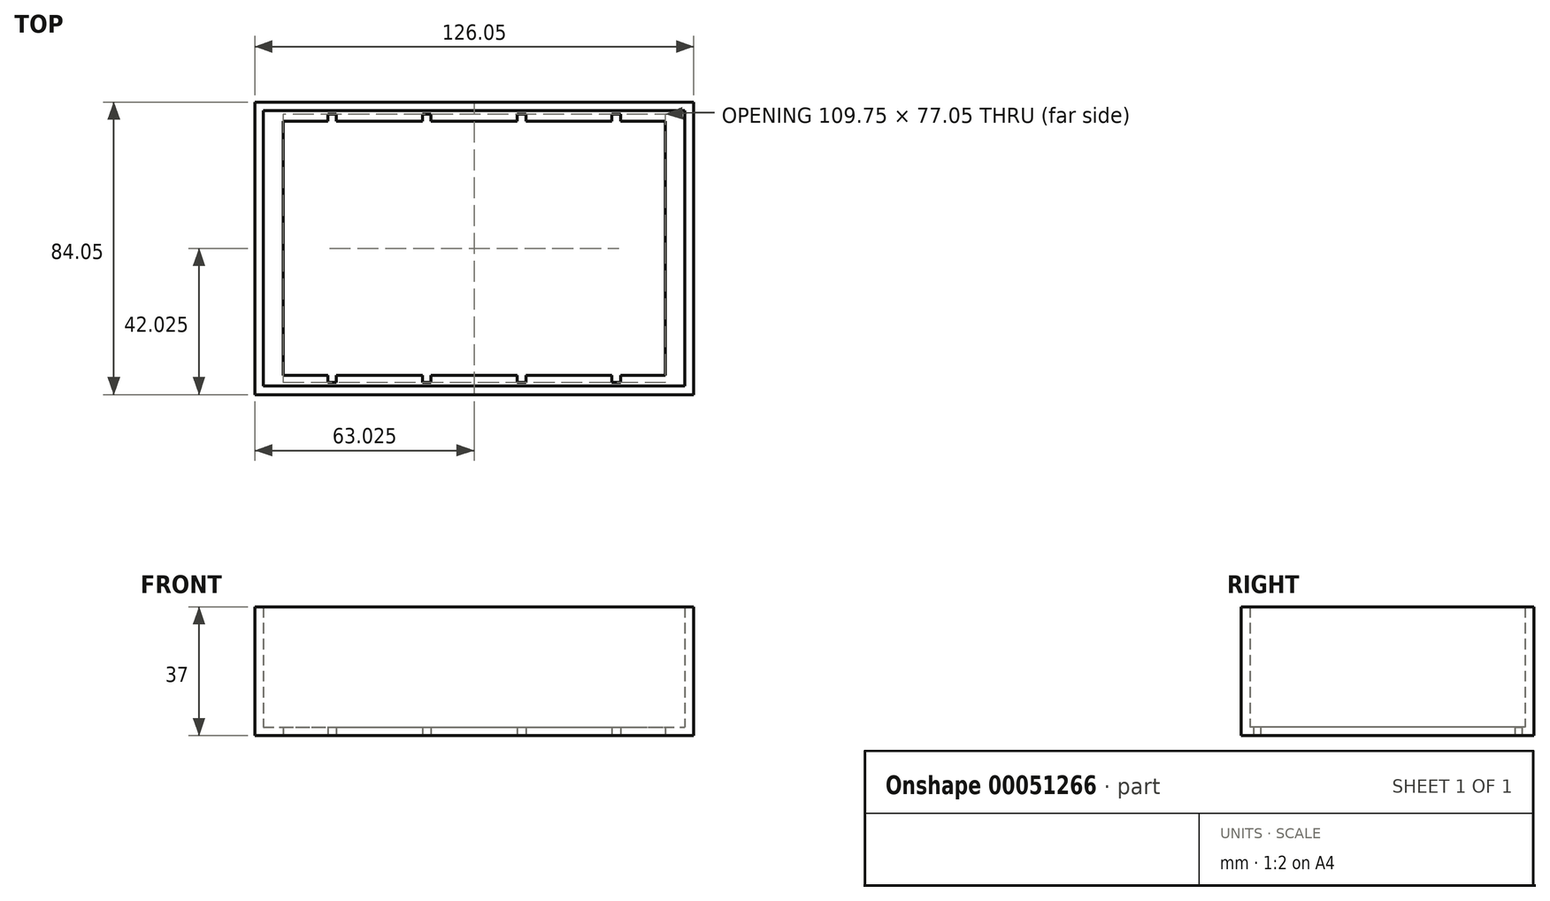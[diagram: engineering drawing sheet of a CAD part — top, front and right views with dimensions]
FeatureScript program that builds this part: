
annotation { "Feature Type Name" : "Feature", "Feature Type Description" : "" }
export const myFeature = defineFeature(function(context is Context, id is Id, definition is map)
    precondition{}
    {
        {
            var Q0;
            Q0=qCreatedBy(makeId("Top.planeOp"),FACE);
            var sketch = newSketch(context, id + "F0", { "sketchPlane" : qUnion([Q0])});
            skLineSegment(sketch, "E0.bottom", {"start": v(0, 0) * mm, "end": v(126.05, 0) * mm});
            skLineSegment(sketch, "E0.top", {"start": v(0, -84.05) * mm, "end": v(126.05, -84.05) * mm});
            skLineSegment(sketch, "E0.left", {"start": v(0, 0) * mm, "end": v(0, -84.05) * mm});
            skLineSegment(sketch, "E0.right", {"start": v(126.05, 0) * mm, "end": v(126.05, -84.05) * mm});
            skLineSegment(sketch, "E1.bottom", {"start": v(2.5, -2.5) * mm, "end": v(123.55, -2.5) * mm});
            skLineSegment(sketch, "E1.top", {"start": v(2.5, -81.55) * mm, "end": v(123.55, -81.55) * mm});
            skLineSegment(sketch, "E1.left", {"start": v(2.5, -2.5) * mm, "end": v(2.5, -81.55) * mm});
            skLineSegment(sketch, "E1.right", {"start": v(123.55, -2.5) * mm, "end": v(123.55, -81.55) * mm});
            skLineSegment(sketch, "E2.bottom", {"start": v(8.15, -5.5) * mm, "end": v(117.9, -5.5) * mm});
            skLineSegment(sketch, "E2.top", {"start": v(8.15, -78.55) * mm, "end": v(117.9, -78.55) * mm});
            skLineSegment(sketch, "E2.left", {"start": v(8.15, -5.5) * mm, "end": v(8.15, -78.55) * mm});
            skLineSegment(sketch, "E2.right", {"start": v(117.9, -5.5) * mm, "end": v(117.9, -78.55) * mm});
            skLineSegment(sketch, "E3.bottom", {"start": v(20.95, -78.55) * mm, "end": v(23.45, -78.55) * mm});
            skLineSegment(sketch, "E3.top", {"start": v(20.95, -80.55) * mm, "end": v(23.45, -80.55) * mm});
            skLineSegment(sketch, "E3.left", {"start": v(20.95, -78.55) * mm, "end": v(20.95, -80.55) * mm});
            skLineSegment(sketch, "E3.right", {"start": v(23.45, -78.55) * mm, "end": v(23.45, -80.55) * mm});
            skLineSegment(sketch, "E4.bottom", {"start": v(20.95, -5.5) * mm, "end": v(23.45, -5.5) * mm});
            skLineSegment(sketch, "E4.top", {"start": v(20.95, -3.5) * mm, "end": v(23.45, -3.5) * mm});
            skLineSegment(sketch, "E4.left", {"start": v(20.95, -5.5) * mm, "end": v(20.95, -3.5) * mm});
            skLineSegment(sketch, "E4.right", {"start": v(23.45, -5.5) * mm, "end": v(23.45, -3.5) * mm});
            skLineSegment(sketch, "E5.bottom", {"start": v(102.6, -78.55) * mm, "end": v(105.1, -78.55) * mm});
            skLineSegment(sketch, "E5.top", {"start": v(102.6, -80.55) * mm, "end": v(105.1, -80.55) * mm});
            skLineSegment(sketch, "E5.left", {"start": v(105.1, -78.55) * mm, "end": v(105.1, -80.55) * mm});
            skLineSegment(sketch, "E5.right", {"start": v(102.6, -78.55) * mm, "end": v(102.6, -80.55) * mm});
            skLineSegment(sketch, "E6.bottom", {"start": v(102.6, -5.5) * mm, "end": v(105.1, -5.5) * mm});
            skLineSegment(sketch, "E6.top", {"start": v(102.6, -3.5) * mm, "end": v(105.1, -3.5) * mm});
            skLineSegment(sketch, "E6.left", {"start": v(102.6, -5.5) * mm, "end": v(102.6, -3.5) * mm});
            skLineSegment(sketch, "E6.right", {"start": v(105.1, -5.5) * mm, "end": v(105.1, -3.5) * mm});
            skLineSegment(sketch, "E7.bottom", {"start": v(48.15, -78.55) * mm, "end": v(50.65, -78.55) * mm});
            skLineSegment(sketch, "E7.top", {"start": v(48.15, -80.55) * mm, "end": v(50.65, -80.55) * mm});
            skLineSegment(sketch, "E7.left", {"start": v(48.15, -78.55) * mm, "end": v(48.15, -80.55) * mm});
            skLineSegment(sketch, "E7.right", {"start": v(50.65, -78.55) * mm, "end": v(50.65, -80.55) * mm});
            skLineSegment(sketch, "E8.bottom", {"start": v(75.4, -78.55) * mm, "end": v(77.9, -78.55) * mm});
            skLineSegment(sketch, "E8.top", {"start": v(75.4, -80.55) * mm, "end": v(77.9, -80.55) * mm});
            skLineSegment(sketch, "E8.left", {"start": v(75.4, -78.55) * mm, "end": v(75.4, -80.55) * mm});
            skLineSegment(sketch, "E8.right", {"start": v(77.9, -78.55) * mm, "end": v(77.9, -80.55) * mm});
            skLineSegment(sketch, "E9.bottom", {"start": v(48.15, -5.5) * mm, "end": v(50.65, -5.5) * mm});
            skLineSegment(sketch, "E9.top", {"start": v(48.15, -3.5) * mm, "end": v(50.65, -3.5) * mm});
            skLineSegment(sketch, "E9.left", {"start": v(48.15, -5.5) * mm, "end": v(48.15, -3.5) * mm});
            skLineSegment(sketch, "E9.right", {"start": v(50.65, -5.5) * mm, "end": v(50.65, -3.5) * mm});
            skLineSegment(sketch, "E10.bottom", {"start": v(75.4, -5.5) * mm, "end": v(77.9, -5.5) * mm});
            skLineSegment(sketch, "E10.top", {"start": v(75.4, -3.5) * mm, "end": v(77.9, -3.5) * mm});
            skLineSegment(sketch, "E10.left", {"start": v(75.4, -5.5) * mm, "end": v(75.4, -3.5) * mm});
            skLineSegment(sketch, "E10.right", {"start": v(77.9, -5.5) * mm, "end": v(77.9, -3.5) * mm});
            skSolve(sketch);
        }
        {
            var Q0;
            Q0=makeQuery(id+"F0.imprint","IMPRINT",FACE,{"disambiguationData":[TD([[makeQuery(id+"F0.imprint","IMPRINT",EDGE,{"derivedFrom":sQuery(id+"F0.wireOp",EDGE,"E1.bottom")}),-1.0]])]});
            extrude(context, id + "F1", {"entities" : qUnion([Q0]), "depth" : 2.5 * mm});
        }
        {
            var Q0;
            Q0=makeQuery(id+"F0.imprint","IMPRINT",FACE,{"disambiguationData":[TD([[makeQuery(id+"F0.imprint","IMPRINT",EDGE,{"derivedFrom":sQuery(id+"F0.wireOp",EDGE,"E0.bottom")}),-1.0]])]});
            extrude(context, id + "F2", {"entities" : qUnion([Q0]), "operationType" : NewBodyOperationType.ADD, "depth" : 37 * mm});
        }
    });
